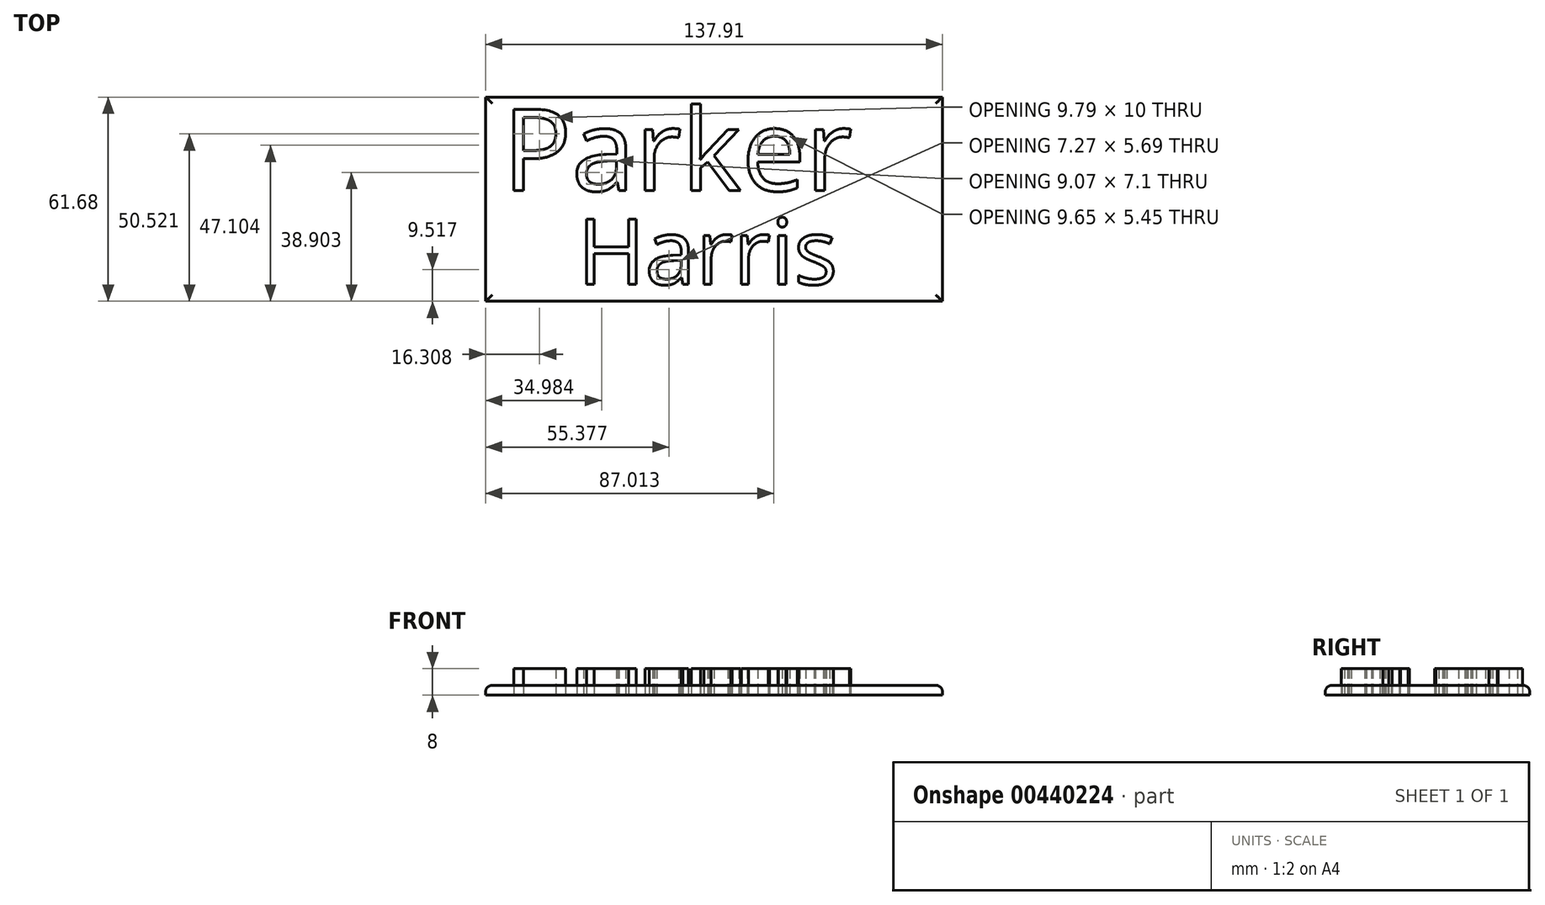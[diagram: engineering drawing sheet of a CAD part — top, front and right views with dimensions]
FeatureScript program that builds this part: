
annotation { "Feature Type Name" : "Feature", "Feature Type Description" : "" }
export const myFeature = defineFeature(function(context is Context, id is Id, definition is map)
    precondition{}
    {
        {
            var Q0;
            Q0=qCreatedBy(makeId("Top.planeOp"),FACE);
            var sketch = newSketch(context, id + "F0", { "sketchPlane" : qUnion([Q0])});
            skText(sketch, "E0", { "text": "Parker", "fontName": "OpenSans-Regular.ttf"});
            const initialGuessF0  = {"E0": [-0.06524, 0.00099, 1, 0, 0.02483]};
            skSetInitialGuess(sketch, initialGuessF0);
            skSolve(sketch);
        }
        {
            var Q0;
            Q0=qCreatedBy(makeId("Top.planeOp"),FACE);
            var sketch = newSketch(context, id + "F1", { "sketchPlane" : qUnion([Q0])});
            skText(sketch, "E1", { "text": "Harris", "fontName": "OpenSans-Regular.ttf"});
            const initialGuessF1  = {"E1": [-0.04268, -0.0273, 1, 0, 0.0199]};
            skSetInitialGuess(sketch, initialGuessF1);
            skSolve(sketch);
        }
        {
            var Q0;
            Q0 = qSketchRegion(id + "F1", true);
            var Q1;
            Q1 = qSketchRegion(id + "F0", true);
            extrude(context, id + "F2", {"entities" : qUnion([Q0, Q1]), "depth" : 8 * mm});
        }
        {
            var Q0;
            Q0=qCreatedBy(makeId("Top.planeOp"),FACE);
            var sketch = newSketch(context, id + "F3", { "sketchPlane" : qUnion([Q0])});
            skLineSegment(sketch, "E2.bottom", {"start": v(-70.4, 29.29) * mm, "end": v(67.5, 29.29) * mm});
            skLineSegment(sketch, "E2.top", {"start": v(-70.4, -32.4) * mm, "end": v(67.5, -32.4) * mm});
            skLineSegment(sketch, "E2.left", {"start": v(-70.4, 29.29) * mm, "end": v(-70.4, -32.4) * mm});
            skLineSegment(sketch, "E2.right", {"start": v(67.5, 29.29) * mm, "end": v(67.5, -32.4) * mm});
            skSolve(sketch);
        }
        {
            var Q0;
            Q0=makeQuery(id+"F3.imprint","IMPRINT",FACE,{"disambiguationData":[TD([[makeQuery(id+"F3.imprint","IMPRINT",EDGE,{"derivedFrom":sQuery(id+"F3.wireOp",EDGE,"E2.bottom")}),-1.0]])]});
            extrude(context, id + "F4", {"entities" : qUnion([Q0]), "depth" : 3 * mm});
        }
        {
            var Q0;
            Q0=makeQuery(id+"F4.opExtrude","CAP_EDGE",EDGE,{"disambiguationData":[OSD([sQuery(id+"F3.wireOp",EDGE,"E2.top")])],"isStart":false});
            var Q1;
            Q1=makeQuery(id+"F4.opExtrude","CAP_EDGE",EDGE,{"disambiguationData":[OSD([sQuery(id+"F3.wireOp",EDGE,"E2.right")])],"isStart":false});
            var Q2;
            Q2=makeQuery(id+"F4.opExtrude","CAP_EDGE",EDGE,{"disambiguationData":[OSD([sQuery(id+"F3.wireOp",EDGE,"E2.bottom")])],"isStart":false});
            var Q3;
            Q3=makeQuery(id+"F4.opExtrude","CAP_EDGE",EDGE,{"disambiguationData":[OSD([sQuery(id+"F3.wireOp",EDGE,"E2.left")])],"isStart":false});
            fillet(context, id + "F5", {"entities" : qUnion([Q0, Q1, Q2, Q3]), "radius" : 2 * mm, "tangentPropagation" : true, "allowEdgeOverflow" : false});
        }
    });
